# Revit family: result
name_source: partatom
category: Generic Models
revit_build: Autodesk Revit 2015 (Build: 20140903_1530(x64)
units: mm (PartAtom-declared; Revit-internal decimal feet)

## types (1)
- Default
    BIMobject category = Tables
    BIMobject category code = tables
    BIMobject main category = Furniture
    BIMobject main category code = furniture
    Brand url = https://www.svedholm.se
    Design country = Sweden
    Edition number = 1
    IFC Classification = Furniture
    Manufacturer country = Sweden
    Manufacturer name = Svedholm
    Material main = Glass
    Material secondary = Powder coated steel
    OmniClass Code = 23-21 23 00
    OmniClass Description = Residential Furniture and Equipment
    Product Guid = 580ac5d6-eec7-4b5d-b44b-ce7b912a4b50
    Product SKU = Urca
    Product data url = https://bimobject.com
    Product family = Urca hourglass-shaped wire
    Product group = Tables
    Product name = Urca
    Product url = https://www.svedholm.se
    QR code = http://bimobject.com
    UNSPSC Code = 56
    Uniclass 1.4 Code = L8221
    Uniclass 1.4 Description = Tables

## geometry (parser evidence)
native form markers: Sweep x2
no freeform markers — native parametric forms only
